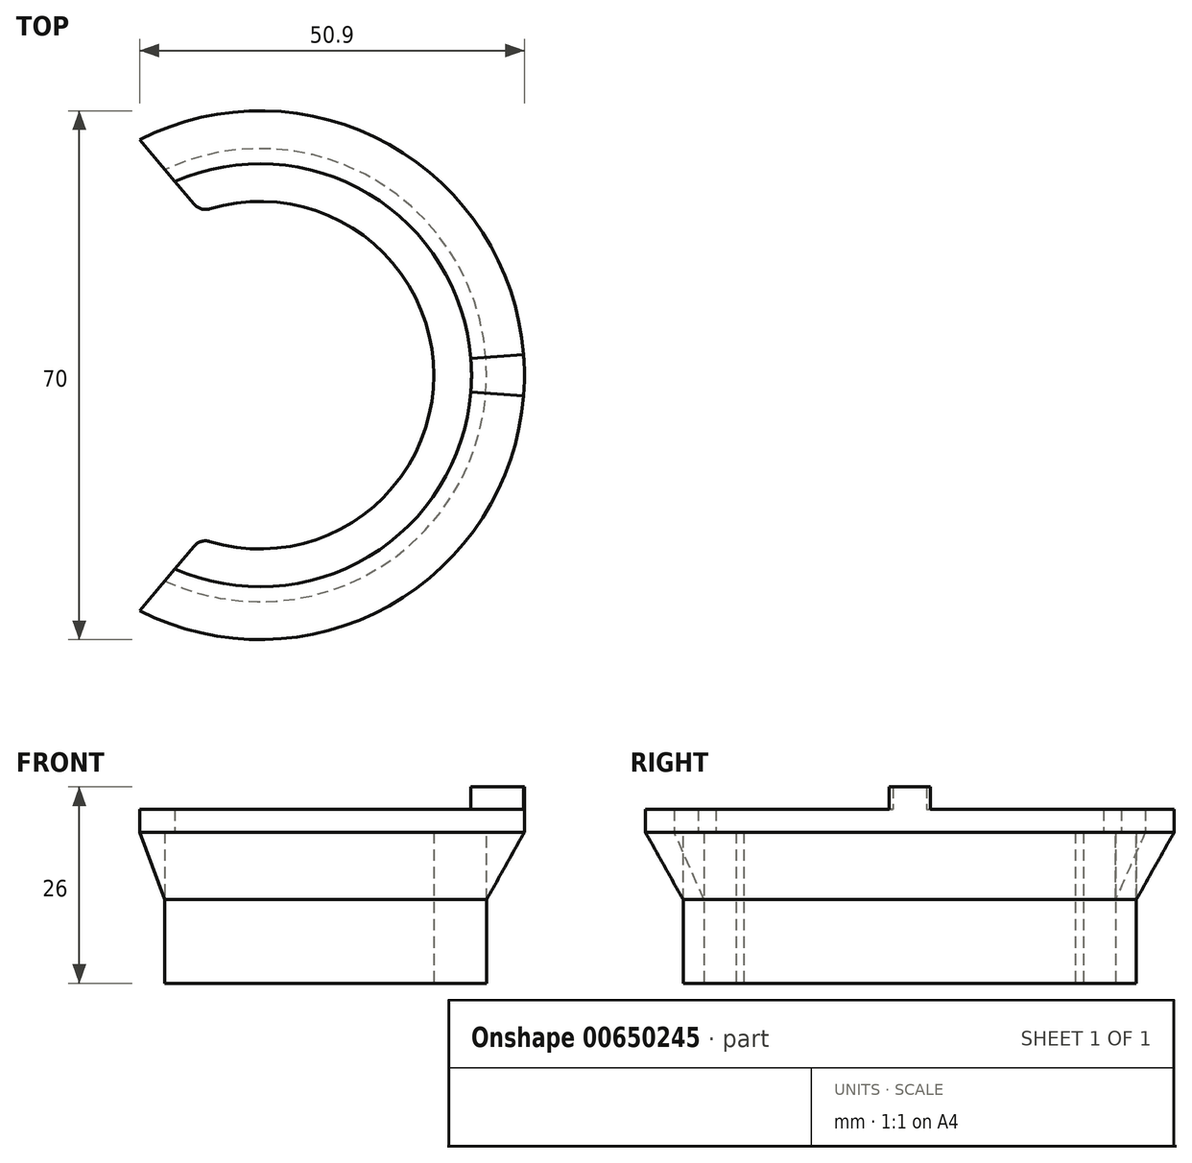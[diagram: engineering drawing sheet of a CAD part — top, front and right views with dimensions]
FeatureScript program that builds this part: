
annotation { "Feature Type Name" : "Feature", "Feature Type Description" : "" }
export const myFeature = defineFeature(function(context is Context, id is Id, definition is map)
    precondition{}
    {
        {
            var Q0;
            Q0=qCreatedBy(makeId("Top.planeOp"),FACE);
            var sketch = newSketch(context, id + "F0", { "sketchPlane" : qUnion([Q0])});
            skArc(sketch, "E0", {"start": v(23, 0) * mm, "mid": v(13.2, 18.84) * mm, "end": v(-7.87, 21.61) * mm});
            skLineSegment(sketch, "E1", {"start": v(0, 0) * mm, "end": v(49.48, 0) * mm, "construction": true});
            skArc(sketch, "E2", {"start": v(30, 0) * mm, "mid": v(16.16, 25.27) * mm, "end": v(-12.58, 27.23) * mm});
            skLineSegment(sketch, "E3", {"start": v(0, 0) * mm, "end": v(-14.53, 39.91) * mm, "construction": true});
            skLineSegment(sketch, "E4", {"start": v(-7.87, 21.61) * mm, "end": v(-12.58, 27.23) * mm});
            skArc(sketch, "E5.MirrorCS", {"start": v(23, 0) * mm, "mid": v(13.2, -18.84) * mm, "end": v(-7.87, -21.61) * mm});
            skArc(sketch, "E6.MirrorCS", {"start": v(30, 0) * mm, "mid": v(16.16, -25.27) * mm, "end": v(-12.58, -27.23) * mm});
            skLineSegment(sketch, "E7.MirrorCS", {"start": v(-7.87, -21.61) * mm, "end": v(-12.58, -27.23) * mm});
            skSolve(sketch);
        }
        {
            var Q0;
            Q0 = qSketchRegion(id + "F0", true);
            extrude(context, id + "F1", {"entities" : qUnion([Q0]), "depth" : 20 * mm, "offsetDistance" : 25 * mm});
        }
        {
            var Q0;
            Q0=makeQuery(id+"F1.opExtrude","CAP_FACE",FACE,{"disambiguationData":[OSD([sQuery(id+"F0.wireOp",EDGE,"E0"),sQuery(id+"F0.wireOp",EDGE,"E2"),sQuery(id+"F0.wireOp",EDGE,"E4"),sQuery(id+"F0.wireOp",EDGE,"E5.MirrorCS"),sQuery(id+"F0.wireOp",EDGE,"E6.MirrorCS"),sQuery(id+"F0.wireOp",EDGE,"E7.MirrorCS")])],"isStart":false});
            var sketch = newSketch(context, id + "F2", { "sketchPlane" : qUnion([Q0])});
            skArc(sketch, "E8.0", {"start": v(-11.25, 25.64) * mm, "mid": v(28, 0) * mm, "end": v(-11.25, -25.64) * mm});
            skLineSegment(sketch, "E9.0", {"start": v(-7.87, 21.61) * mm, "end": v(-18.84, 34.69) * mm, "construction": true});
            skLineSegment(sketch, "E10.0", {"start": v(-7.87, -21.61) * mm, "end": v(-14.31, -29.3) * mm, "construction": true});
            skArc(sketch, "E11", {"start": v(-15.9, -31.18) * mm, "mid": v(35, 0) * mm, "end": v(-15.9, 31.18) * mm});
            skLineSegment(sketch, "E12", {"start": v(-11.25, -25.64) * mm, "end": v(-15.9, -31.18) * mm});
            skLineSegment(sketch, "E13", {"start": v(-11.25, 25.64) * mm, "end": v(-15.9, 31.18) * mm});
            skSolve(sketch);
        }
        {
            var Q0;
            Q0 = qSketchRegion(id + "F2", true);
            extrude(context, id + "F3", {"entities" : qUnion([Q0]), "depth" : 3 * mm, "offsetDistance" : 25 * mm});
        }
        {
            var Q0;
            Q0=makeQuery(id+"F1.opExtrude","SWEPT_FACE",FACE,{"disambiguationData":[OSD([sQuery(id+"F0.wireOp",EDGE,"E7.MirrorCS")])]});
            var sketch = newSketch(context, id + "F4", { "sketchPlane" : qUnion([Q0])});
            skLineSegment(sketch, "E14.0", {"start": v(28.95, 20) * mm, "end": v(28.95, 11.07) * mm});
            skLineSegment(sketch, "E15.0", {"start": v(26.87, 20) * mm, "end": v(34.1, 20) * mm});
            skLineSegment(sketch, "E16", {"start": v(28.95, 11.07) * mm, "end": v(34.1, 20) * mm});
            skPoint(sketch, "E17.orphan", {"position": v(28.95, 0) * mm});
            skPoint(sketch, "E18.orphan", {"position": v(34.1, 20) * mm});
            skSolve(sketch);
        }
        {
            var Q0;
            Q0 = qSketchRegion(id + "F4", true);
            var Q1;
            Q1=makeQuery(id+"F3.opExtrude","CAP_EDGE",EDGE,{"disambiguationData":[OSD([sQuery(id+"F2.wireOp",EDGE,"E11")])],"isStart":true});
            sweep(context, id + "F5", {"profiles" : qUnion([Q0]), "path" : qUnion([Q1])});
        }
        {
            var Q0;
            Q0=makeQuery(id+"F3.opExtrude","CAP_FACE",FACE,{"disambiguationData":[OSD([sQuery(id+"F2.wireOp",EDGE,"E8.0"),sQuery(id+"F2.wireOp",EDGE,"E11"),sQuery(id+"F2.wireOp",EDGE,"E12"),sQuery(id+"F2.wireOp",EDGE,"E13")])],"isStart":false});
            var sketch = newSketch(context, id + "F6", { "sketchPlane" : qUnion([Q0])});
            skPoint(sketch, "E19.0", {"position": v(0, 0) * mm});
            skLineSegment(sketch, "E20", {"start": v(0, 0) * mm, "end": v(27.91, 2.2) * mm, "construction": true});
            skArc(sketch, "E21.1", {"start": v(27.91, 2.2) * mm, "mid": v(27.98, 1.1) * mm, "end": v(28, 0) * mm});
            skArc(sketch, "E22.0", {"start": v(35, 0) * mm, "mid": v(34.97, 1.38) * mm, "end": v(34.9, 2.75) * mm});
            skLineSegment(sketch, "E23", {"start": v(27.91, 2.2) * mm, "end": v(34.9, 2.75) * mm});
            skPoint(sketch, "E24", {"position": v(28, 0) * mm});
            skPoint(sketch, "E25.orphan", {"position": v(-6.62, -27.2) * mm});
            skPoint(sketch, "E26.orphan", {"position": v(-6.62, 27.2) * mm});
            skPoint(sketch, "E27", {"position": v(35, 0) * mm});
            skPoint(sketch, "E28.orphan", {"position": v(-10.24, -33.47) * mm});
            skPoint(sketch, "E29.orphan", {"position": v(-10.24, 33.47) * mm});
            skLineSegment(sketch, "E30.trimOffspring", {"start": v(34.9, 2.75) * mm, "end": v(36.83, 2.9) * mm, "construction": true});
            skArc(sketch, "E31.MirrorCS", {"start": v(35, 0) * mm, "mid": v(34.97, -1.38) * mm, "end": v(34.9, -2.75) * mm});
            skLineSegment(sketch, "E32.MirrorCS", {"start": v(27.91, -2.2) * mm, "end": v(34.9, -2.75) * mm});
            skArc(sketch, "E33.MirrorCS", {"start": v(27.91, -2.2) * mm, "mid": v(27.98, -1.1) * mm, "end": v(28, 0) * mm});
            skSolve(sketch);
        }
        {
            var Q0;
            Q0 = qSketchRegion(id + "F6", true);
            extrude(context, id + "F7", {"entities" : qUnion([Q0]), "operationType" : NewBodyOperationType.ADD, "depth" : 3 * mm, "offsetDistance" : 25 * mm});
        }
        {
            var Q0;
            Q0=makeQuery(id+"F1.opExtrude","SWEPT_EDGE",EDGE,{"disambiguationData":[OSD([sQuery(id+"F0.wireOp",EDGE,"E0"),sQuery(id+"F0.wireOp",EDGE,"E4")])]});
            fillet(context, id + "F8", {"entities" : qUnion([Q0]), "radius" : 2 * mm, "tangentPropagation" : true, "allowEdgeOverflow" : false});
        }
        {
            var Q0;
            Q0=makeQuery(id+"F1.opExtrude","SWEPT_EDGE",EDGE,{"disambiguationData":[OSD([sQuery(id+"F0.wireOp",EDGE,"E5.MirrorCS"),sQuery(id+"F0.wireOp",EDGE,"E7.MirrorCS")])]});
            fillet(context, id + "F9", {"entities" : qUnion([Q0]), "radius" : 2 * mm, "tangentPropagation" : true, "allowEdgeOverflow" : false});
        }
        {
            var Q0;
            {var subQ0=sQuery(id+"F2.wireOp",EDGE,"E11");var subQ1=sQuery(id+"F2.wireOp",EDGE,"E13");var subQ2=sQuery(id+"F2.wireOp",EDGE,"E8.0");Q0=makeQuery(id+"F7.boolean.opBoolean","SPLIT",FACE,{"disambiguationData":[TD([makeQuery(id+"F3.opExtrude","SWEPT_FACE",FACE,{"disambiguationData":[OSD([subQ1])]})])],"derivedFrom":makeQuery(id+"F3.opExtrude","CAP_FACE",FACE,{"disambiguationData":[OSD([subQ2,subQ0,sQuery(id+"F2.wireOp",EDGE,"E12"),subQ1])],"isStart":false})});}
            var sketch = newSketch(context, id + "F10", { "sketchPlane" : qUnion([Q0])});
            skLineSegment(sketch, "E34.0", {"start": v(-11.25, 25.64) * mm, "end": v(-15.9, 31.18) * mm});
            skLineSegment(sketch, "E35", {"start": v(-15.9, 31.18) * mm, "end": v(-25.99, 26.04) * mm});
            skLineSegment(sketch, "E36", {"start": v(-11.25, 25.64) * mm, "end": v(-21.74, 19.36) * mm});
            skLineSegment(sketch, "E37", {"start": v(-21.74, 19.36) * mm, "end": v(-25.99, 26.04) * mm});
            skSolve(sketch);
        }
        {
            var Q0;
            Q0 = qSketchRegion(id + "F10", true);
            extrude(context, id + "F11", {"entities" : qUnion([Q0]), "operationType" : NewBodyOperationType.REMOVE, "oppositeDirection" : true, "depth" : 25 * mm, "offsetDistance" : 25 * mm});
        }
    });
